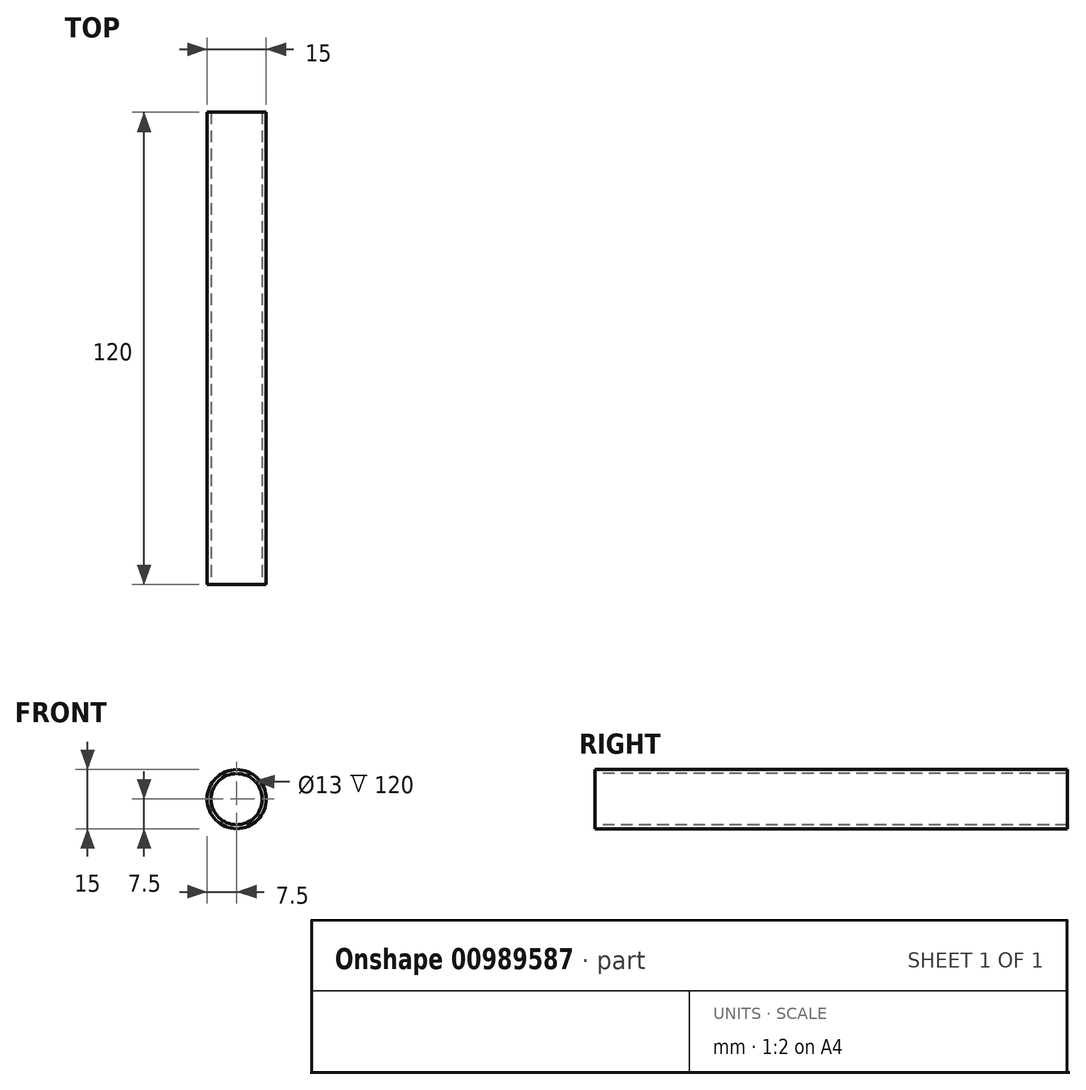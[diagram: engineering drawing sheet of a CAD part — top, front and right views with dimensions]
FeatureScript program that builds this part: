
annotation { "Feature Type Name" : "Feature", "Feature Type Description" : "" }
export const myFeature = defineFeature(function(context is Context, id is Id, definition is map)
    precondition{}
    {
        {
            var Q0;
            Q0=qCreatedBy(makeId("Front.planeOp"),FACE);
            var sketch = newSketch(context, id + "F0", { "sketchPlane" : qUnion([Q0])});
            skCircle(sketch, "E0", {"center": v(0, 0) * mm, "radius": 7.5 * mm});
            skCircle(sketch, "E1", {"center": v(0, 0) * mm, "radius": 6.5 * mm});
            skSolve(sketch);
        }
        {
            var Q0;
            Q0 = qSketchRegion(id + "F0", true);
            extrude(context, id + "F1", {"entities" : qUnion([Q0]), "oppositeDirection" : true, "depth" : 120 * mm, "offsetDistance" : 25 * mm});
        }
    });
